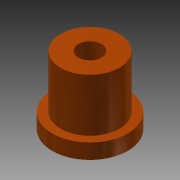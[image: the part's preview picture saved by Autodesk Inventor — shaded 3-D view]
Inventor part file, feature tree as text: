
AUTODESK INVENTOR PART (.ipt)
format: ipt  version: 2013 (Build 170138000, 138)  size: 89,088 bytes
history: native  units: mm
features: extrude x3, sketch x3
ambient origin geometry x8: Origin, YZ Plane, XZ Plane, XY Plane, X Axis, Y Axis, Z Axis, Center Point
bodies: Solid1 (feature_tree)
feature tree (6):
  extrude  "Extrusion1"  Depth=2.0mm TaperAngle=0.0deg
  extrude  "Extrusion2"  Depth=7.0mm TaperAngle=0.0deg
  extrude  "Extrusion3"  Depth=7.0mm TaperAngle=0.0deg
  sketch  "Sketch1"  dims[d0=10.0mm d2=2.0mm d3=0.0mm]
  sketch  "Sketch2"  dims[d4=7.8mm d7=7.0mm d8=0.0mm]
  sketch  "Sketch3"  dims[d9=3.1mm d11=7.0mm d12=0.0mm]
